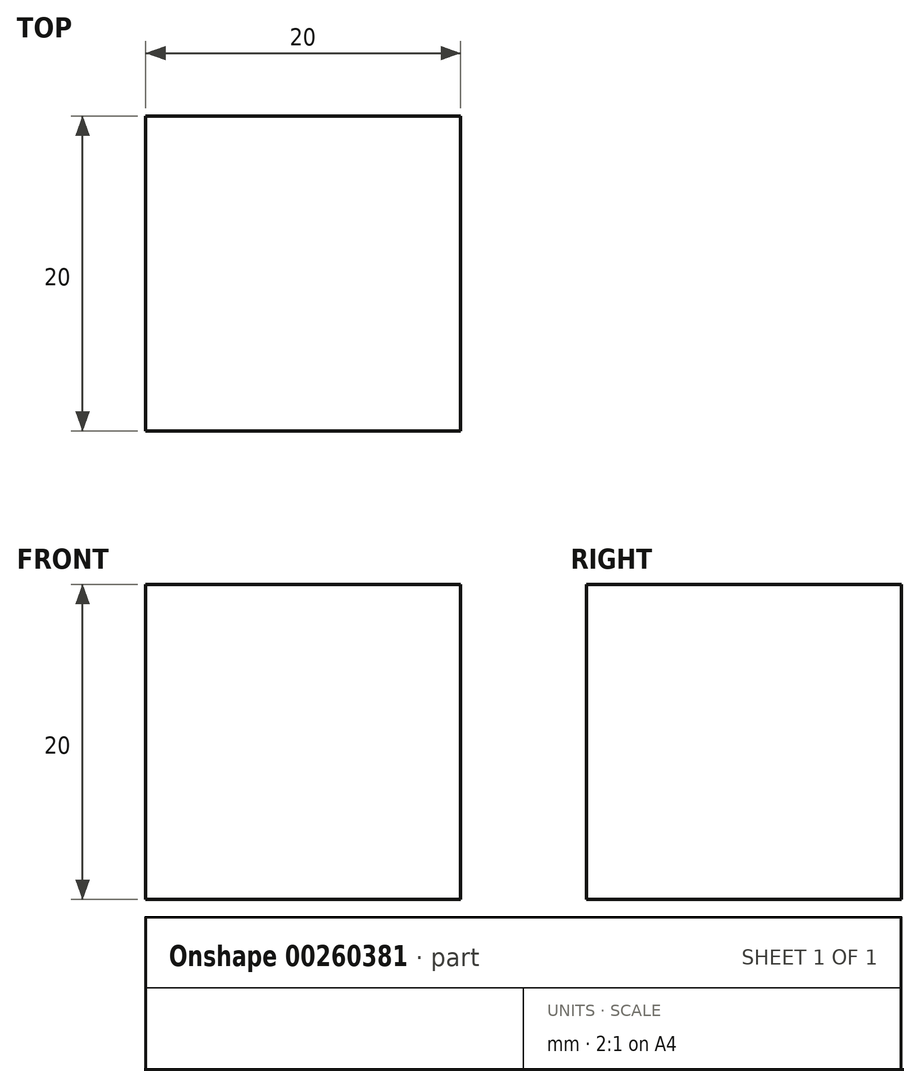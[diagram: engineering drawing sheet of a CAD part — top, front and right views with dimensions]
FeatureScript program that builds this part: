
annotation { "Feature Type Name" : "Feature", "Feature Type Description" : "" }
export const myFeature = defineFeature(function(context is Context, id is Id, definition is map)
    precondition{}
    {
        {
            var Q0;
            Q0=qCreatedBy(makeId("Top.planeOp"),FACE);
            var sketch = newSketch(context, id + "F0", { "sketchPlane" : qUnion([Q0])});
            skPoint(sketch, "E0.middle", {"position": v(0, 0) * mm});
            skLineSegment(sketch, "E1.bottom", {"start": v(10, 10) * mm, "end": v(-10, 10) * mm});
            skLineSegment(sketch, "E1.top", {"start": v(10, -10) * mm, "end": v(-10, -10) * mm});
            skLineSegment(sketch, "E1.left", {"start": v(10, 10) * mm, "end": v(10, -10) * mm});
            skLineSegment(sketch, "E1.right", {"start": v(-10, 10) * mm, "end": v(-10, -10) * mm});
            skSolve(sketch);
        }
        {
            var Q0;
            Q0 = qSketchRegion(id + "F0", true);
            extrude(context, id + "F1", {"entities" : qUnion([Q0]), "endBound" : BoundingType.SYMMETRIC, "depth" : 20 * mm});
        }
    });
